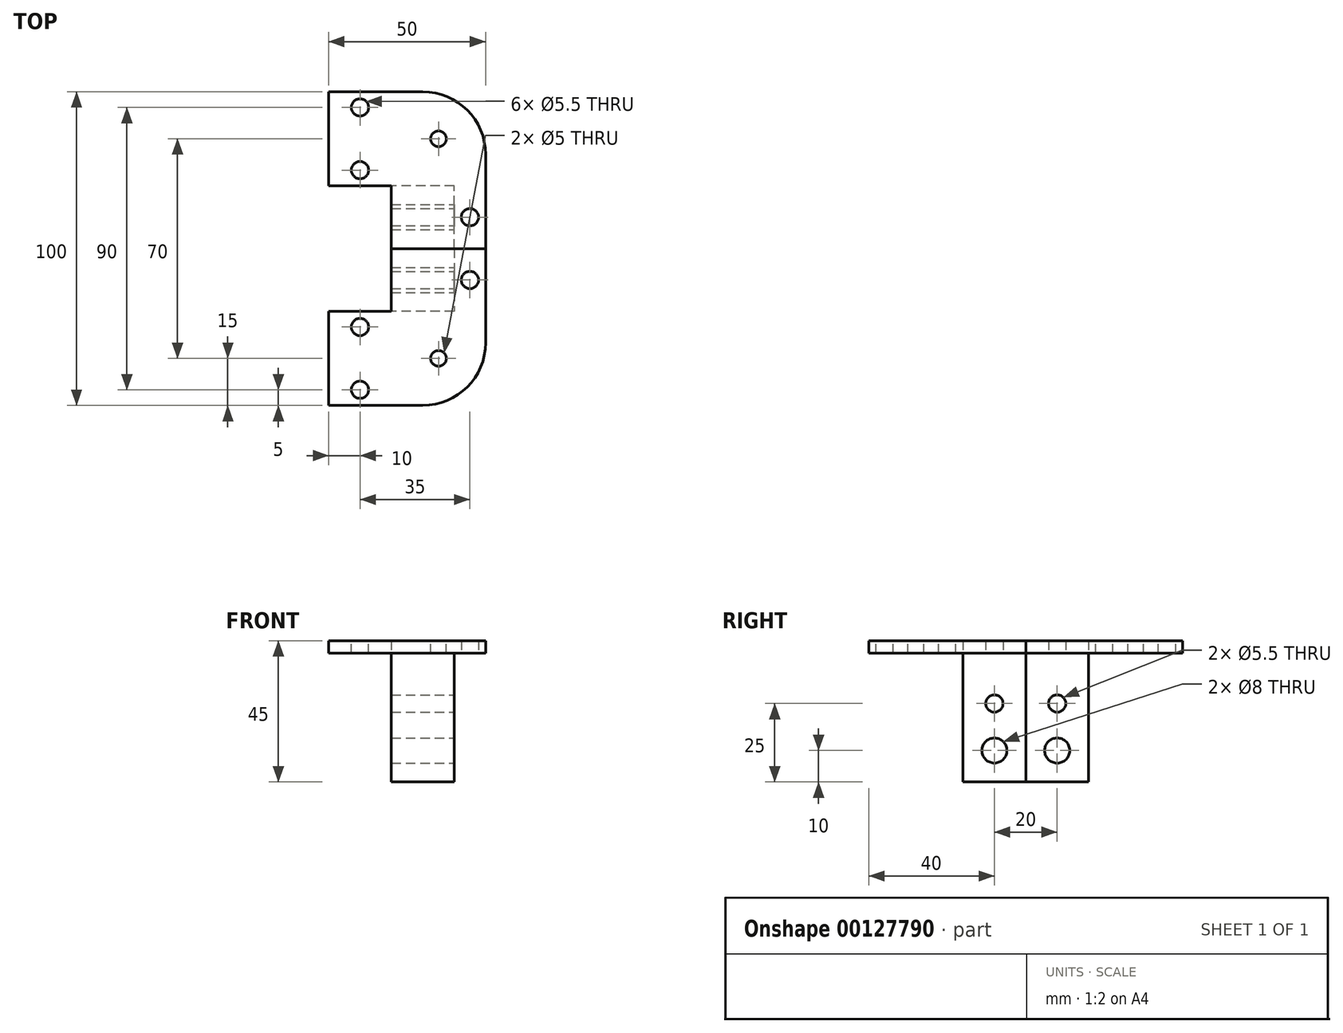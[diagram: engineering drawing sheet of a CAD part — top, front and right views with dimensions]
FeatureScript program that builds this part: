
annotation { "Feature Type Name" : "Feature", "Feature Type Description" : "" }
export const myFeature = defineFeature(function(context is Context, id is Id, definition is map)
    precondition{}
    {
        {
            var Q0;
            Q0=qCreatedBy(makeId("Top.planeOp"),FACE);
            var sketch = newSketch(context, id + "F0", { "sketchPlane" : qUnion([Q0])});
            skLineSegment(sketch, "E0.bottom", {"start": v(15, -15) * mm, "end": v(-15, -15) * mm});
            skLineSegment(sketch, "E0.top", {"start": v(15, 15) * mm, "end": v(-15, 15) * mm});
            skLineSegment(sketch, "E0.left", {"start": v(15, -15) * mm, "end": v(15, 15) * mm});
            skLineSegment(sketch, "E0.right", {"start": v(-15, -15) * mm, "end": v(-15, 15) * mm});
            skPoint(sketch, "E0.middle", {"position": v(0, 0) * mm});
            skSolve(sketch);
        }
        {
            var Q0;
            Q0=makeQuery(id+"F0.imprint","IMPRINT",FACE,{"disambiguationData":[TD([[makeQuery(id+"F0.imprint","IMPRINT",EDGE,{"derivedFrom":sQuery(id+"F0.wireOp",EDGE,"E0.bottom")}),-1.0]])]});
            extrude(context, id + "F1", {"entities" : qUnion([Q0]), "endBound" : BoundingType.SYMMETRIC, "depth" : 4 * mm});
        }
        {
            var Q0;
            Q0=makeQuery(id+"F1.opExtrude","SWEPT_FACE",FACE,{"disambiguationData":[OSD([sQuery(id+"F0.wireOp",EDGE,"E0.right")])]});
            extrude(context, id + "F2", {"entities" : qUnion([Q0]), "operationType" : NewBodyOperationType.ADD, "depth" : 20 * mm});
        }
        {
            var Q0;
            {var subQ0=sQuery(id+"F0.wireOp",EDGE,"E0.right");Q0=makeQuery(id+"F2.boolean.opBoolean","MERGE",FACE,{"derivedFrom":[makeQuery(id+"F1.opExtrude","CAP_FACE",FACE,{"disambiguationData":[OSD([sQuery(id+"F0.wireOp",EDGE,"E0.bottom"),sQuery(id+"F0.wireOp",EDGE,"E0.top"),sQuery(id+"F0.wireOp",EDGE,"E0.left"),subQ0])],"isStart":false}),makeQuery(id+"F2.opExtrude","SWEPT_FACE",FACE,{"disambiguationData":[OSD([subQ0]),TDD([makeQuery(id+"F1.opExtrude","CAP_EDGE",EDGE,{"disambiguationData":[OSD([subQ0])],"isStart":false})])]})]});}
            var sketch = newSketch(context, id + "F3", { "sketchPlane" : qUnion([Q0])});
            skLineSegment(sketch, "E1", {"start": v(0, 0) * mm, "end": v(-48.41, 0) * mm, "construction": true});
            skCircle(sketch, "E2", {"center": v(-25, 10) * mm, "radius": 2.75 * mm});
            skCircle(sketch, "E3.MirrorC", {"center": v(-25, -10) * mm, "radius": 2.75 * mm});
            skSolve(sketch);
        }
        {
            var Q0;
            Q0=qSketchRegion(id+"F3",true);
            extrude(context, id + "F4", {"entities" : qUnion([Q0]), "operationType" : NewBodyOperationType.REMOVE, "endBound" : BoundingType.THROUGH_ALL, "oppositeDirection" : true, "depth" : 25 * mm});
        }
        {
            var Q0;
            {var subQ0=sQuery(id+"F0.wireOp",EDGE,"E0.top");Q0=makeQuery(id+"F2.boolean.opBoolean","MERGE",FACE,{"derivedFrom":[makeQuery(id+"F1.opExtrude","SWEPT_FACE",FACE,{"disambiguationData":[OSD([subQ0])]}),makeQuery(id+"F2.opExtrude","SWEPT_FACE",FACE,{"disambiguationData":[OSD([subQ0,sQuery(id+"F0.wireOp",EDGE,"E0.right")])]})]});}
            var sketch = newSketch(context, id + "F5", { "sketchPlane" : qUnion([Q0])});
            skLineSegment(sketch, "E4.bottom", {"start": v(15, 2) * mm, "end": v(-5, 2) * mm});
            skLineSegment(sketch, "E4.top", {"start": v(15, -43) * mm, "end": v(-5, -43) * mm});
            skLineSegment(sketch, "E4.left", {"start": v(15, 2) * mm, "end": v(15, -43) * mm});
            skLineSegment(sketch, "E4.right", {"start": v(-5, 2) * mm, "end": v(-5, -43) * mm});
            skSolve(sketch);
        }
        {
            var Q0;
            Q0=qSketchRegion(id+"F5",true);
            extrude(context, id + "F6", {"entities" : qUnion([Q0]), "operationType" : NewBodyOperationType.ADD, "depth" : 20 * mm});
        }
        {
            var Q0;
            {var subQ0=sQuery(id+"F0.wireOp",EDGE,"E0.left");var subQ1=sQuery(id+"F0.wireOp",EDGE,"E0.right");var subQ2=sQuery(id+"F0.wireOp",EDGE,"E0.top");Q0=makeQuery(id+"F6.boolean.opBoolean","SPLIT",FACE,{"disambiguationData":[TD([makeQuery(id+"F1.opExtrude","SWEPT_FACE",FACE,{"disambiguationData":[OSD([subQ0])]})])],"derivedFrom":makeQuery(id+"F2.boolean.opBoolean","MERGE",FACE,{"derivedFrom":[makeQuery(id+"F1.opExtrude","SWEPT_FACE",FACE,{"disambiguationData":[OSD([subQ2])]}),makeQuery(id+"F2.opExtrude","SWEPT_FACE",FACE,{"disambiguationData":[OSD([subQ2,subQ1])]})]})});}
            var Q1;
            Q1=makeQuery(id+"F6.opExtrude","CAP_FACE",FACE,{"disambiguationData":[OSD([sQuery(id+"F5.wireOp",EDGE,"E4.bottom"),sQuery(id+"F5.wireOp",EDGE,"E4.top"),sQuery(id+"F5.wireOp",EDGE,"E4.left"),sQuery(id+"F5.wireOp",EDGE,"E4.right")])],"isStart":false});
            extrude(context, id + "F7", {"entities" : qUnion([Q0]), "operationType" : NewBodyOperationType.ADD, "endBound" : BoundingType.UP_TO_SURFACE, "endBoundEntityFace" : qUnion([Q1]), "depth" : 25 * mm});
        }
        {
            var Q0;
            Q0=makeQuery(id+"F6.opExtrude","SWEPT_FACE",FACE,{"disambiguationData":[OSD([sQuery(id+"F5.wireOp",EDGE,"E4.right")])]});
            var sketch = newSketch(context, id + "F8", { "sketchPlane" : qUnion([Q0])});
            skCircle(sketch, "E5", {"center": v(25, -33) * mm, "radius": 4 * mm});
            skLineSegment(sketch, "E6", {"start": v(25, -33) * mm, "end": v(25, -43) * mm, "construction": true});
            skCircle(sketch, "E7", {"center": v(25, -18) * mm, "radius": 2.75 * mm});
            skSolve(sketch);
        }
        {
            var Q0;
            Q0=qSketchRegion(id+"F8",true);
            extrude(context, id + "F9", {"entities" : qUnion([Q0]), "operationType" : NewBodyOperationType.REMOVE, "endBound" : BoundingType.THROUGH_ALL, "oppositeDirection" : true, "depth" : 25 * mm});
        }
        {
            var Q0;
            {var subQ0=sQuery(id+"F0.wireOp",EDGE,"E0.right");var subQ1=sQuery(id+"F0.wireOp",EDGE,"E0.top");var subQ2=sQuery(id+"F0.wireOp",EDGE,"E0.left");var subQ3=makeQuery(id+"F1.opExtrude","CAP_FACE",FACE,{"disambiguationData":[OSD([sQuery(id+"F0.wireOp",EDGE,"E0.bottom"),subQ1,subQ2,subQ0])],"isStart":true});var subQ4=sQuery(id+"F5.wireOp",EDGE,"E4.right");var subQ5=makeQuery(id+"F2.opExtrude","SWEPT_FACE",FACE,{"disambiguationData":[OSD([subQ0]),TDD([makeQuery(id+"F1.opExtrude","CAP_EDGE",EDGE,{"disambiguationData":[OSD([subQ0])],"isStart":true})])]});Q0=makeQuery(id+"F7.boolean.opBoolean","MERGE",FACE,{"derivedFrom":[makeQuery(id+"F2.boolean.opBoolean","MERGE",FACE,{"derivedFrom":[subQ3,subQ5]}),makeQuery(id+"F7.opExtrude","SWEPT_FACE",FACE,{"disambiguationData":[OSD([subQ1,subQ0]),TDD([makeQuery(id+"F6.boolean.opBoolean","SPLIT",EDGE,{"disambiguationData":[TD([subQ3,makeQuery(id+"F1.opExtrude","SWEPT_FACE",FACE,{"disambiguationData":[OSD([subQ1])]}),makeQuery(id+"F1.opExtrude","SWEPT_FACE",FACE,{"disambiguationData":[OSD([subQ2])]}),makeQuery(id+"F2.opExtrude","SWEPT_FACE",FACE,{"disambiguationData":[OSD([subQ1,subQ0])]}),subQ5,makeQuery(id+"F6.opExtrude","CAP_FACE",FACE,{"disambiguationData":[OSD([sQuery(id+"F5.wireOp",EDGE,"E4.bottom"),sQuery(id+"F5.wireOp",EDGE,"E4.top"),sQuery(id+"F5.wireOp",EDGE,"E4.left"),subQ4])],"isStart":true}),makeQuery(id+"F6.opExtrude","SWEPT_FACE",FACE,{"disambiguationData":[OSD([subQ4])]})])],"derivedFrom":makeQuery(id+"F2.boolean.opBoolean","MERGE",EDGE,{"derivedFrom":[makeQuery(id+"F1.opExtrude","CAP_EDGE",EDGE,{"disambiguationData":[OSD([subQ1])],"isStart":true}),makeQuery(id+"F2.opExtrude","SWEPT_EDGE",EDGE,{"disambiguationData":[OSD([subQ1,subQ0]),TDD([makeQuery(id+"F1.opExtrude","CAP_VERTEX",VERTEX,{"disambiguationData":[OSD([subQ1,subQ0])],"isStart":true})])]})]})})])]})]});}
            var sketch = newSketch(context, id + "F10", { "sketchPlane" : qUnion([Q0])});
            skCircle(sketch, "E8", {"center": v(10, -25) * mm, "radius": 2.75 * mm});
            skLineSegment(sketch, "E9", {"start": v(10, -25) * mm, "end": v(5, -25) * mm, "construction": true});
            skSolve(sketch);
        }
        {
            var Q0;
            Q0=qSketchRegion(id+"F10",true);
            extrude(context, id + "F11", {"entities" : qUnion([Q0]), "operationType" : NewBodyOperationType.REMOVE, "endBound" : BoundingType.THROUGH_ALL, "oppositeDirection" : true, "depth" : 25 * mm});
        }
        {
            var Q0;
            {var subQ0=sQuery(id+"F0.wireOp",EDGE,"E0.right");var subQ1=sQuery(id+"F0.wireOp",EDGE,"E0.top");var subQ2=sQuery(id+"F0.wireOp",EDGE,"E0.left");var subQ3=makeQuery(id+"F2.opExtrude","SWEPT_FACE",FACE,{"disambiguationData":[OSD([subQ0]),TDD([makeQuery(id+"F1.opExtrude","CAP_EDGE",EDGE,{"disambiguationData":[OSD([subQ0])],"isStart":false})])]});var subQ4=makeQuery(id+"F1.opExtrude","CAP_FACE",FACE,{"disambiguationData":[OSD([sQuery(id+"F0.wireOp",EDGE,"E0.bottom"),subQ1,subQ2,subQ0])],"isStart":false});var subQ5=makeQuery(id+"F6.opExtrude","SWEPT_FACE",FACE,{"disambiguationData":[OSD([sQuery(id+"F5.wireOp",EDGE,"E4.bottom")])]});Q0=makeQuery(id+"F7.boolean.opBoolean","MERGE",FACE,{"derivedFrom":[makeQuery(id+"F6.boolean.opBoolean","MERGE",FACE,{"derivedFrom":[makeQuery(id+"F2.boolean.opBoolean","MERGE",FACE,{"derivedFrom":[subQ4,subQ3]}),subQ5]}),makeQuery(id+"F7.opExtrude","SWEPT_FACE",FACE,{"disambiguationData":[OSD([subQ1,subQ0]),TDD([makeQuery(id+"F6.boolean.opBoolean","SPLIT",EDGE,{"disambiguationData":[TD([makeQuery(id+"F1.opExtrude","SWEPT_FACE",FACE,{"disambiguationData":[OSD([subQ2])]})])],"derivedFrom":makeQuery(id+"F2.boolean.opBoolean","MERGE",EDGE,{"derivedFrom":[makeQuery(id+"F1.opExtrude","CAP_EDGE",EDGE,{"disambiguationData":[OSD([subQ1])],"isStart":false}),makeQuery(id+"F2.opExtrude","SWEPT_EDGE",EDGE,{"disambiguationData":[OSD([subQ1,subQ0]),TDD([makeQuery(id+"F1.opExtrude","CAP_VERTEX",VERTEX,{"disambiguationData":[OSD([subQ1,subQ0])],"isStart":false})])]})]})})])]})]});}
            var sketch = newSketch(context, id + "F12", { "sketchPlane" : qUnion([Q0])});
            skLineSegment(sketch, "E10", {"start": v(-15, 15) * mm, "end": v(-15, -15) * mm, "construction": true});
            skLineSegment(sketch, "E11", {"start": v(-15, 15) * mm, "end": v(15, 15) * mm, "construction": true});
            skCircle(sketch, "E12", {"center": v(0, 0) * mm, "radius": 2.5 * mm});
            skSolve(sketch);
        }
        {
            var Q0;
            Q0 = qSketchRegion(id + "F12", true);
            extrude(context, id + "F13", {"entities" : qUnion([Q0]), "operationType" : NewBodyOperationType.REMOVE, "endBound" : BoundingType.THROUGH_ALL, "oppositeDirection" : true, "depth" : 25 * mm});
        }
        {
            var Q0;
            Q0=makeQuery(id+"F1.opExtrude","SWEPT_EDGE",EDGE,{"disambiguationData":[OSD([sQuery(id+"F0.wireOp",EDGE,"E0.bottom"),sQuery(id+"F0.wireOp",EDGE,"E0.left")])]});
            fillet(context, id + "F14", {"entities" : qUnion([Q0]), "radius" : 20 * mm, "tangentPropagation" : true, "allowEdgeOverflow" : false});
        }
        {
            var Q0;
            Q0=makeQuery(id+"F1.opExtrude","SWEPT_BODY",BODY,{"disambiguationData":[OSD([sQuery(id+"F0.wireOp",EDGE,"E0.bottom"),sQuery(id+"F0.wireOp",EDGE,"E0.top"),sQuery(id+"F0.wireOp",EDGE,"E0.left"),sQuery(id+"F0.wireOp",EDGE,"E0.right")])]});
            var Q1;
            {var subQ0=sQuery(id+"F5.wireOp",EDGE,"E4.right");var subQ1=sQuery(id+"F5.wireOp",EDGE,"E4.left");var subQ2=sQuery(id+"F5.wireOp",EDGE,"E4.top");var subQ3=sQuery(id+"F5.wireOp",EDGE,"E4.bottom");Q1=makeQuery(id+"F7.boolean.opBoolean","MERGE",FACE,{"derivedFrom":[makeQuery(id+"F6.opExtrude","CAP_FACE",FACE,{"disambiguationData":[OSD([subQ3,subQ2,subQ1,subQ0])],"isStart":false}),makeQuery(id+"F7.opExtrude","CAP_FACE",FACE,{"disambiguationData":[OSD([subQ3,subQ2,subQ1,subQ0])],"isStart":false})]});}
            mirror(context, id + "F15", {"entities" : qUnion([Q0]), "mirrorPlane" : qUnion([Q1])});
        }
    });
